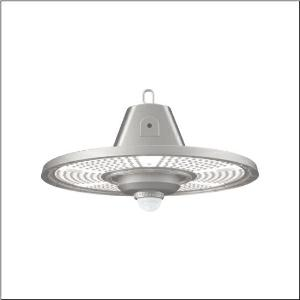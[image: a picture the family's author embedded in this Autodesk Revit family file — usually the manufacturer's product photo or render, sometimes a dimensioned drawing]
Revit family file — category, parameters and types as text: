
# Revit family: highbay_31-l_51hc427a4mmb01
name_source: partatom
category: Lighting Fixtures
units: mm (PartAtom-declared; Revit-internal decimal feet)

## family parameters
Cut with Voids When Loaded = No
Host = Face
Light Source = No
Part Type = Normal
Room Calculation Point = No
Round Connector Dimension = Use Diameter
Shared = No

## types (1)
- Highbay 31-L (1 x LED, 28000 lm, 187 W, 4000K)
    Apparent Load = 187 VA
    CIE Flux Codes = 83 98 100 100 100
    Color Rendering = 80
    Color Temperature = 4000K
    Default Elevation = 1800 mm
    Description = Highbay 31-L, LED high bay luminaire, primary light control with lens, of PC, primary optical cover: cover panel, of PC, transparent, light emission: direct distribution, primary light characteristic: rotationally symmetric, installation type: suspended mounting, surface-mounted, LED, rated luminous flux: 28.000lm, luminous efficacy: 150lm/W, light colour: 840, colour temperature: 4000K, control gear: ECG, with cable, 3x 1.0mm², free wire ends, mains connection: 220..240V, AC/DC, 0/50..60Hz, cable length: 1,5m, rated input power: 187W, housing, rotationally symmetric, of diecast aluminium, powder-coated, grey aluminium (RAL 9007), with hook on luminaire side, incl. screw, diameter: 406mm, PIR sensor, protection rating (complete): IP65, insulation class (complete): insulation class I (protective earthing), certification: CE, ENEC, UKCA, protection symbol: D, impact resistance: IK08, permissible operating ambient temperature: -30..+45°C, standard: EN 60598-2-22, EN 60598, corresponds to IFS (International Featured Standards) requirements for safety and quality in the food industry, packaging unit: 1 piece
    Height = 160 mm
    Lamp = 1 x LED
    Lamp Light Flux = 28000 lm
    Lamp Power = 187 W
    Lamp count = 1
    Length = 406 mm
    Luminous efficacy = 150 lm/W
    Manufacturer = Siteco
    ModVariant = No
    Model = 51HC427A4MMB01
    Mounting Place = Ceiling
    Mounting Type = Pendant
    Number of Poles = 1
    OnlyDefault = Yes
    Power Factor = 1
    Product Name = Highbay 31-L
    Product group = LED high bay luminaire
    ProductGroupID = 903
    Protection Class = Protection class I
    Protection Degree = IP 65
    RLX_Detail_Level = 1
    RLX_Emergency_Light_Flux = 0 lm
    RLX_Emergency_Type = 0
    RLX_Emergency_Type_DB = No
    RlxData = <blob elided: 120969 chars, md5=bd546bdc>
    Socket = socket
    Standby Power = 0 W
    System Light Flux = 28000 lm
    System Power = 187 W
    Type Comments = Product without accessories
    Type Image = l_384981.jpg
    URL = http://relux.com
    VarID = ---
    Voltage = 0 V
    Weight = 0.00 kg
    Width = 0 mm  [stored 0 ft]

note: [stored X ft] marks values corroborated as IEEE doubles in the binary element streams (Revit-internal decimal feet)

## geometry (parser evidence)
native form markers: Blend x4, Sweep x11
no freeform markers — native parametric forms only
